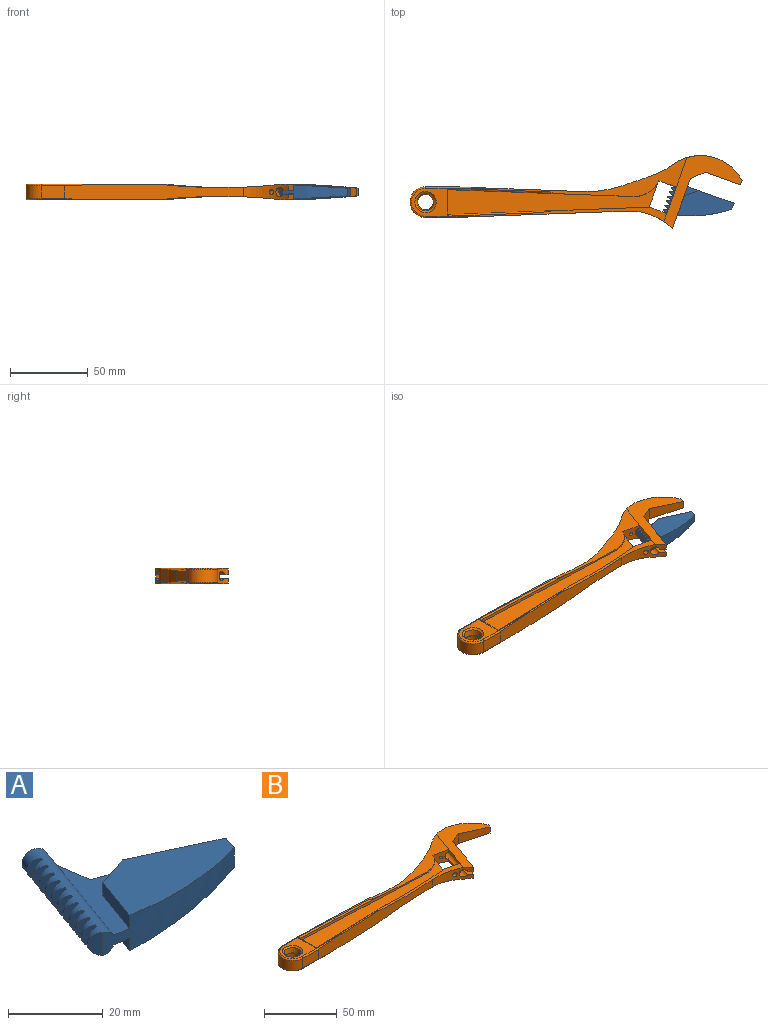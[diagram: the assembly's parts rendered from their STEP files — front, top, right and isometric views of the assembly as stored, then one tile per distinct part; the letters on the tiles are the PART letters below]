
ASSEMBLY  parts=2 mates=1
PART A: 47 faces, bbox 46.1x34.5x9.1 mm
  f0: plane 5.89x2.99mm, normal (0,1,0), area 13.7mm2, adj f1,f32
  f1: plane 5.89x0.47mm, normal (-0.94,0.34,0), area 2.9mm2, adj f0,f2,f32
  f2: plane 5.89x2.3mm, normal (-0.64,-0.77,0), area 13.7mm2, adj f1,f32
  f3: plane 5.89x2.99mm, normal (0,1,0), area 13.7mm2, adj f4,f32
  f4: plane 5.89x0.47mm, normal (-0.94,0.34,0), area 2.9mm2, adj f3,f5,f32
  f5: plane 5.89x2.3mm, normal (-0.64,-0.77,0), area 13.7mm2, adj f4,f32
  f6: plane 5.89x2.99mm, normal (0,1,0), area 13.7mm2, adj f7,f32
  f7: plane 5.89x0.47mm, normal (-0.94,0.34,0), area 2.9mm2, adj f6,f8,f32
  f8: plane 5.89x2.3mm, normal (-0.64,-0.77,0), area 13.7mm2, adj f7,f32
  f9: plane 5.89x2.99mm, normal (0,1,0), area 13.7mm2, adj f10,f32
  f10: plane 5.89x0.47mm, normal (-0.94,0.34,0), area 2.9mm2, adj f9,f11,f32
  f11: plane 5.89x2.3mm, normal (-0.64,-0.77,0), area 13.7mm2, adj f10,f32
  f12: plane 5.89x2.99mm, normal (0,1,0), area 13.7mm2, adj f13,f32
  f13: plane 5.89x0.47mm, normal (-0.94,0.34,0), area 2.9mm2, adj f12,f14,f32
  f14: plane 5.89x2.3mm, normal (-0.64,-0.77,0), area 13.7mm2, adj f13,f32
  f15: plane 5.89x2.99mm, normal (0,1,0), area 13.7mm2, adj f16,f32
  f16: plane 5.89x0.47mm, normal (-0.94,0.34,0), area 2.9mm2, adj f15,f17,f32
  f17: plane 5.89x2.3mm, normal (-0.64,-0.77,0), area 13.7mm2, adj f16,f32
  f18: plane 5.89x2.99mm, normal (0,1,0), area 13.7mm2, adj f19,f32
  f19: plane 5.89x0.47mm, normal (-0.94,0.34,0), area 2.9mm2, adj f18,f20,f32
  f20: plane 5.89x2.3mm, normal (-0.64,-0.77,0), area 13.7mm2, adj f19,f32
  f21: plane 5.89x2.99mm, normal (0,1,0), area 13.7mm2, adj f22,f32
  f22: plane 5.89x0.47mm, normal (-0.94,0.34,0), area 2.9mm2, adj f21,f23,f32
  f23: plane 5.89x2.3mm, normal (-0.64,-0.77,0), area 13.7mm2, adj f22,f32
  f24: plane 5.89x2.99mm, normal (0,1,0), area 13.7mm2, adj f25,f32
  f25: plane 5.89x0.47mm, normal (-0.94,0.34,0), area 2.9mm2, adj f24,f26,f32
  f26: plane 5.89x2.3mm, normal (-0.64,-0.77,0), area 13.7mm2, adj f25,f32
  f27: plane 36.44x16.36mm, normal (0.06,-0.02,1), area 396.8mm2, adj f28,f30,f35,f39,f41
  f28: plane 29.77x10.76mm, normal (0.34,0.94,0), area 177.5mm2, adj f27,f30,f31,f33,f34,f37,f40,f41
  f29: plane 12.57x4.54mm, normal (-0.94,0.34,0), area 44.3mm2, adj f33,f34,f39,f40
  f30: plane 5x3.72mm, normal (0.94,-0.34,0), area 19.8mm2, adj f27,f28,f34,f39
  f31: plane 27.26x17.95mm, normal (0,0,1), area 123mm2, adj f28,f32,f35,f37,f39,f41
  f32: cylinder r=2.95mm len=33.89mm, axis (0.34,0.94,0), area 370mm2, adj f0,f1,f2,f3,f4,f5,f6,f7
  f33: plane 27.26x17.95mm, normal (0,0,-1), area 123mm2, adj f28,f29,f32,f37,f39,f40
  f34: plane 36.44x16.36mm, normal (0.06,-0.02,-1), area 396.8mm2, adj f28,f29,f30,f39,f40
  f35: plane 12.57x4.54mm, normal (-0.94,0.34,0), area 44.3mm2, adj f27,f31,f39,f41
  f36: plane 5.9x5.29mm, normal (0.34,0.94,0), area 26.9mm2, adj f32,f38
  f37: plane 8.83x2.51mm, normal (0.99,0.14,0), area 22.3mm2, adj f28,f31,f33,f38
  f38: plane 4.85x2.51mm, normal (0.94,-0.34,0), area 12.9mm2, adj f32,f36,f37
  f39: cylinder r=80mm len=42.1mm, axis (0,0,1), area 273.8mm2, adj f27,f29,f30,f31,f32,f33,f34,f35
  f40: plane 9.21x3.32mm, normal (-0.34,0.94,0), area 30mm2, adj f28,f29,f33,f34
  f41: plane 9.21x3.32mm, normal (-0.34,0.94,0), area 30mm2, adj f27,f28,f31,f35
  f42: plane 5.89x2.99mm, normal (0,1,0), area 13.7mm2, adj f32,f43
  f43: plane 5.89x0.47mm, normal (-0.94,0.34,0), area 2.9mm2, adj f32,f42,f44
  f44: plane 5.89x2.3mm, normal (-0.64,-0.77,0), area 13.7mm2, adj f32,f43
  f45: plane 5.89x2.3mm, normal (-0.64,-0.77,0), area 13.7mm2, adj f32,f46
  f46: plane 5.89x0.24mm, normal (-0.94,0.34,0), area 1.5mm2, adj f32,f39,f45
PART B: 66 faces, bbox 214.5x87.8x10 mm
  f0: plane 5x2.77mm, normal (0.94,-0.34,0), area 14.7mm2, adj f11,f27,f61,f62
  f1: plane 65.48x2.41mm, normal (0,0,1), area 51.8mm2, adj f19,f31,f44,f58
  f2: plane 60.3x2.23mm, normal (0,0,1), area 46.6mm2, adj f18,f24,f45,f56
  f3: plane 65.48x2.41mm, normal (0,0,-1), area 51.8mm2, adj f17,f31,f46,f55
  f4: plane 60.3x2.23mm, normal (0,0,-1), area 46.6mm2, adj f16,f24,f47,f53
  f5: cylinder r=39.62mm len=29.08mm, axis (0,0,-1), area 214.4mm2, adj f6,f24,f25,f45,f47,f48,f49,f51
  f6: plane 32.08x11.59mm, normal (0.94,-0.34,0), area 99.5mm2, adj f5,f26,f49,f61
  f7: plane 17x6.14mm, normal (-0.94,0.34,0), area 36.2mm2, adj f29,f30,f51,f62
  f8: plane 17x6.14mm, normal (-0.94,0.34,0), area 36.2mm2, adj f29,f30,f51,f61
  f9: plane 23x18mm, normal (0,0,-1), area 258.8mm2, adj f42,f53,f54,f55,f64
  f10: plane 23x18mm, normal (0,0,1), area 230.5mm2, adj f43,f56,f57,f58,f65
  f11: cylinder r=30mm len=44.02mm, axis (0,0,-1), area 347.2mm2, adj f0,f12,f44,f46,f48,f49,f50,f51
  f12: cylinder r=60mm len=15.51mm, axis (0,0,-1), area 134.5mm2, adj f11,f28,f44,f46
  f13: cylinder r=70mm len=25.1mm, axis (0,0,-1), area 151.1mm2, adj f28,f31,f44,f46
  f14: cylinder r=17.73mm len=16.7mm, axis (0,0,1), area 31.6mm2, adj f30,f35,f37,f44
  f15: cylinder r=17.73mm len=16.7mm, axis (0,0,-1), area 31.6mm2, adj f30,f40,f41,f46
  f16: cylinder r=1mm len=72.52mm, axis (-1,-0.04,0), area 101.5mm2, adj f4,f38,f42,f47,f53
  f17: cylinder r=1mm len=76.34mm, axis (1,-0.04,0), area 108.2mm2, adj f3,f40,f42,f46,f55
  f18: cylinder r=1mm len=72.52mm, axis (-1,-0.04,0), area 101.5mm2, adj f2,f34,f43,f45,f56
  f19: cylinder r=1mm len=76.34mm, axis (1,-0.04,0), area 108.2mm2, adj f1,f35,f43,f44,f58
  f20: plane 17x6.14mm, normal (0.94,-0.34,0), area 72.3mm2, adj f29,f30,f37,f41
  f21: plane 15x8mm, normal (0,1,0), area 120mm2, adj f22,f31,f55,f58
  f22: cylinder r=10mm len=20mm, axis (0,0,-1), area 251.3mm2, adj f21,f23,f54,f57
  f23: plane 15x8mm, normal (0,-1,0), area 120mm2, adj f22,f24,f53,f56
  f24: plane 114.86x10.03mm, normal (0.04,-1,0), area 960.9mm2, adj f2,f4,f5,f23,f45,f47,f53,f56
  f25: plane 32.08x11.59mm, normal (0.94,-0.34,0), area 126.7mm2, adj f5,f26,f48,f62
  f26: plane 9.5x9.13mm, normal (0.4,-0.92,0), area 80mm2, adj f6,f25,f27,f48,f49,f50,f61,f62
  f27: plane 22.69x8.2mm, normal (-0.34,-0.94,0), area 158.6mm2, adj f0,f26,f61,f62
  f28: plane 17.75x6.79mm, normal (-0.32,0.95,0), area 115.3mm2, adj f12,f13,f44,f46
  f29: plane 11.38x10mm, normal (0.34,0.94,0), area 83.8mm2, adj f7,f8,f20,f34,f38,f45,f47,f51
  f30: plane 11.38x10mm, normal (-0.34,-0.94,0), area 88mm2, adj f7,f8,f14,f15,f20,f44,f46,f51
  f31: plane 86.31x10.01mm, normal (0.04,1,0), area 812.8mm2, adj f1,f3,f13,f21,f44,f46,f55,f58
  f32: cylinder r=5mm len=10mm, axis (0,0,-1), area 116.4mm2, adj f63,f64
  f33: cone r=5mm half-angle=10deg, axis (0,0,1), area 133.9mm2, adj f63,f65
  f34: plane 128.92x4.79mm, normal (-0.04,1,0), area 211.9mm2, adj f18,f29,f36,f37,f45
  f35: plane 118.37x4.4mm, normal (-0.04,-1,0), area 199.3mm2, adj f14,f19,f36,f37,f44
  f36: plane 16x2mm, normal (1,0,0), area 32mm2, adj f34,f35,f37,f43
  f37: plane 135.06x21.78mm, normal (0,0,1), area 1484.1mm2, adj f14,f20,f34,f35,f36
  f38: plane 128.92x4.79mm, normal (-0.04,1,0), area 211.9mm2, adj f16,f29,f39,f41,f47
  f39: plane 16x2mm, normal (1,0,0), area 32mm2, adj f38,f40,f41,f42
  f40: plane 118.37x4.4mm, normal (-0.04,-1,0), area 199.3mm2, adj f15,f17,f39,f41,f46
  f41: plane 135.06x21.78mm, normal (0,0,-1), area 1484.1mm2, adj f15,f20,f38,f39,f40
  f42: cylinder r=1mm len=18.04mm, axis (0,1,0), area 26.3mm2, adj f9,f16,f17,f39,f53,f55
  f43: cylinder r=1mm len=18.04mm, axis (0,1,0), area 26.3mm2, adj f10,f18,f19,f36,f56,f58
  f44: cylinder r=330mm len=88.27mm, axis (0.34,0.94,0), area 514.2mm2, adj f1,f11,f12,f13,f14,f19,f28,f30
  f45: cylinder r=330mm len=80.38mm, axis (0.34,0.94,0), area 199.4mm2, adj f2,f5,f18,f24,f29,f34,f62
  f46: cylinder r=330mm len=88.27mm, axis (0.34,0.94,0), area 514.2mm2, adj f3,f11,f12,f13,f15,f17,f28,f30
  f47: cylinder r=330mm len=80.38mm, axis (0.34,0.94,0), area 199.4mm2, adj f4,f5,f16,f24,f29,f38,f61
  f48: plane 46.92x22.89mm, normal (0,0,-1), area 222.8mm2, adj f5,f11,f25,f26,f50,f51
  f49: plane 46.92x23.19mm, normal (0,0,1), area 240mm2, adj f5,f6,f11,f26,f50,f51
  f50: plane 13.31x4.81mm, normal (-0.94,0.34,0), area 35.4mm2, adj f11,f26,f48,f49
  f51: cylinder r=3mm len=45.76mm, axis (0.34,0.94,0), area 531.9mm2, adj f5,f7,f8,f11,f29,f30,f48,f49
  f52: cylinder r=1.6mm len=5.43mm, axis (-0.34,-0.94,0), area 44.8mm2, adj f5,f29
  f53: cylinder r=1mm len=41.98mm, axis (1,0,0), area 39mm2, adj f4,f9,f16,f23,f24,f42,f54
  f54: torus R=9mm, axis (0,0,1), area 47.6mm2, adj f9,f22,f53,f55
  f55: cylinder r=1mm len=41.98mm, axis (-1,0,0), area 39mm2, adj f3,f9,f17,f21,f31,f42,f54
  f56: cylinder r=1mm len=41.98mm, axis (-1,0,0), area 39mm2, adj f2,f10,f18,f23,f24,f43,f57
  f57: torus R=9mm, axis (0,0,1), area 47.6mm2, adj f10,f22,f56,f58
  f58: cylinder r=1mm len=41.98mm, axis (1,0,0), area 39mm2, adj f1,f10,f19,f21,f31,f43,f57
  f59: cylinder r=1.1mm len=5.45mm, axis (-0.34,-0.94,0), area 34.6mm2, adj f30,f60
  f60: plane 2.2x2.07mm, normal (-0.34,-0.94,0), area 3.8mm2, adj f59
  f61: plane 50.25x46.93mm, normal (0.06,-0.02,-1), area 625.9mm2, adj f0,f5,f6,f8,f11,f26,f27,f46
  f62: plane 50.25x46.93mm, normal (0.06,-0.02,1), area 625.9mm2, adj f0,f5,f7,f11,f25,f26,f27,f44
  f63: cone r=5mm half-angle=5deg, axis (0,0,1), area 6.5mm2, adj f32,f33
  f64: cone r=6.19mm half-angle=45deg, axis (0,0,-1), area 59.3mm2, adj f9,f32
  f65: cone r=6.88mm half-angle=50deg, axis (0,0,1), area 60.6mm2, adj f10,f33
PLACE A t=(-74.84,1.31,-34.48)mm
PLACE B t=(-40.04,-11.85,-17.86)mm fixed
MATE slider A.f32 <-> B.f51  axis (0.34,0.94,0) through (57.47,-19.42,-17.86)mm
